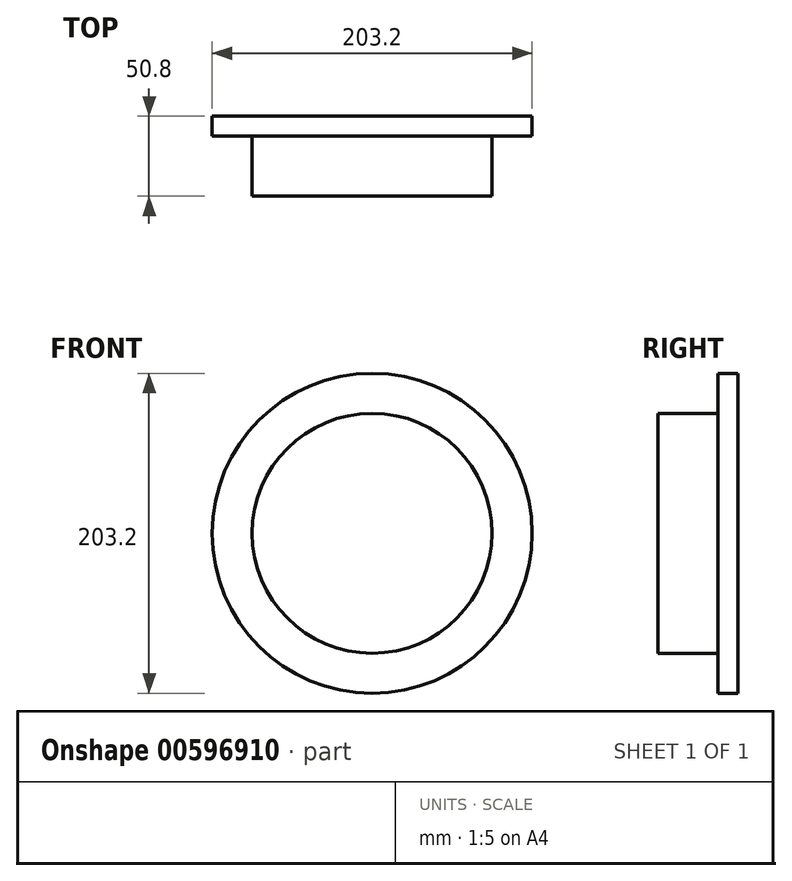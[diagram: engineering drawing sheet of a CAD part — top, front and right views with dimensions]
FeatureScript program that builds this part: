
annotation { "Feature Type Name" : "Feature", "Feature Type Description" : "" }
export const myFeature = defineFeature(function(context is Context, id is Id, definition is map)
    precondition{}
    {
        {
            var Q0;
            Q0=qCreatedBy(makeId("Top.planeOp"),FACE);
            var sketch = newSketch(context, id + "F0", { "sketchPlane" : qUnion([Q0])});
            skLineSegment(sketch, "E0", {"start": v(0, 0) * mm, "end": v(0, 50.8) * mm});
            skLineSegment(sketch, "E1", {"start": v(0, 50.8) * mm, "end": v(101.6, 50.8) * mm});
            skLineSegment(sketch, "E2", {"start": v(101.6, 50.8) * mm, "end": v(101.6, 38.1) * mm});
            skLineSegment(sketch, "E3", {"start": v(101.6, 38.1) * mm, "end": v(76.2, 38.1) * mm});
            skLineSegment(sketch, "E4", {"start": v(76.2, 38.1) * mm, "end": v(76.2, 0) * mm});
            skLineSegment(sketch, "E5", {"start": v(76.2, 0) * mm, "end": v(0, 0) * mm});
            skSolve(sketch);
        }
        {
            var Q0;
            Q0=makeQuery(id+"F0.imprint","IMPRINT",FACE,{"disambiguationData":[TD([[makeQuery(id+"F0.imprint","IMPRINT",EDGE,{"derivedFrom":sQuery(id+"F0.wireOp",EDGE,"E0")}),-1.0]])]});
            var Q1;
            Q1=sQuery(id+"F0.wireOp",EDGE,"E0");
            revolve(context, id + "F1", {"entities" : qUnion([Q0]), "axis" : qUnion([Q1]), "revolveType" : RevolveType.FULL});
        }
    });
